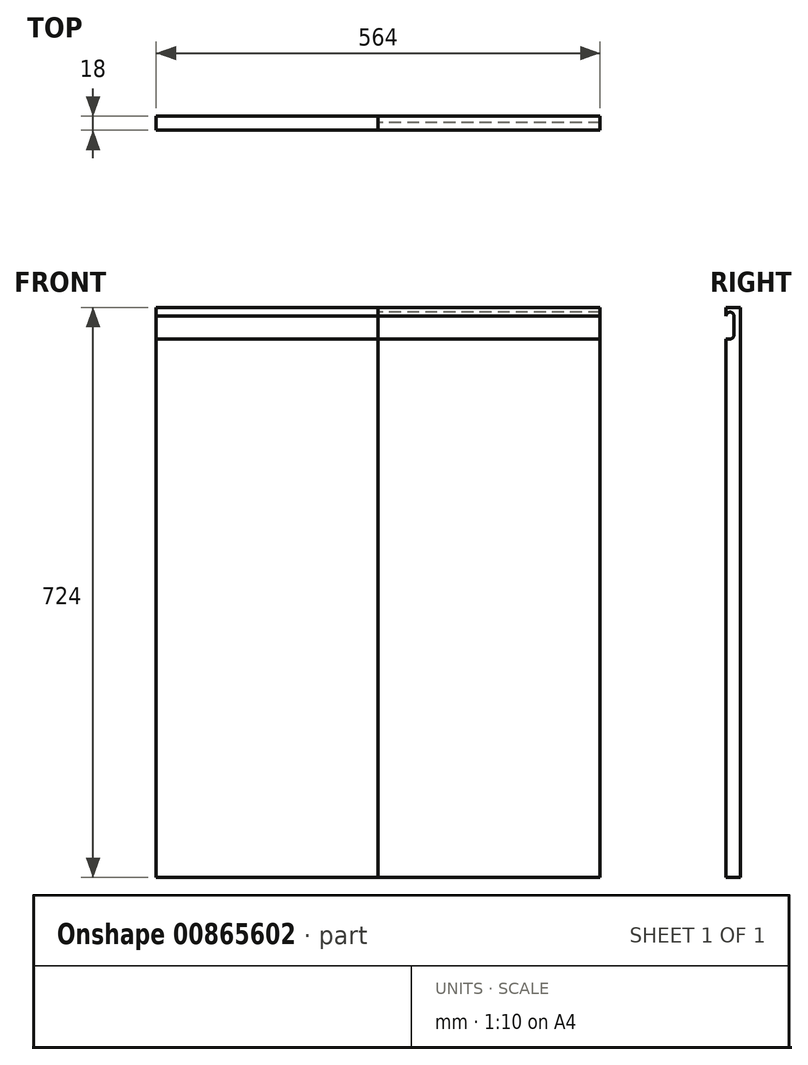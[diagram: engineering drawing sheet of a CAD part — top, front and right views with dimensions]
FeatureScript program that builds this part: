
annotation { "Feature Type Name" : "Feature", "Feature Type Description" : "" }
export const myFeature = defineFeature(function(context is Context, id is Id, definition is map)
    precondition{}
    {
        {
            var Q0;
            Q0=qCreatedBy(makeId("Front.planeOp"),FACE);
            var sketch = newSketch(context, id + "F0", { "sketchPlane" : qUnion([Q0])});
            skLineSegment(sketch, "E0.left", {"start": v(-331.36, 211.7) * mm, "end": v(-331.36, -512.3) * mm});
            skLineSegment(sketch, "E1", {"start": v(-613.36, -512.3) * mm, "end": v(-49.36, -512.3) * mm});
            skLineSegment(sketch, "E2", {"start": v(-613.36, 211.7) * mm, "end": v(-49.36, 211.7) * mm});
            skLineSegment(sketch, "E3", {"start": v(-49.36, 211.7) * mm, "end": v(-49.36, -512.3) * mm});
            skLineSegment(sketch, "E4", {"start": v(-613.36, 211.7) * mm, "end": v(-613.36, -512.3) * mm});
            skPoint(sketch, "E5.orphan", {"position": v(-631.36, 249.7) * mm});
            skSolve(sketch);
        }
        {
            var Q0;
            {var subQ0=sQuery(id+"F0.wireOp",EDGE,"E0.left");Q0=makeQuery(id+"F0.imprint","IMPRINT",FACE,{"disambiguationData":[TD([[makeQuery(id+"F0.imprint","IMPRINT",EDGE,{"derivedFrom":subQ0}),1.0]])]});}
            extrude(context, id + "F1", {"entities" : qUnion([Q0]), "depth" : 18 * mm, "offsetDistance" : 25 * mm});
        }
        {
            var Q0;
            Q0 = qSketchRegion(id + "F0", true);
            extrude(context, id + "F2", {"entities" : qUnion([Q0]), "depth" : 18 * mm, "offsetDistance" : 25 * mm});
        }
        {
            var Q0;
            Q0=makeQuery(id+"F2.opExtrude","SWEPT_FACE",FACE,{"disambiguationData":[OSD([sQuery(id+"F0.wireOp",EDGE,"E4")])]});
            var sketch = newSketch(context, id + "F3", { "sketchPlane" : qUnion([Q0])});
            skLineSegment(sketch, "E6", {"start": v(18, 171.7) * mm, "end": v(13, 171.7) * mm});
            skLineSegment(sketch, "E7", {"start": v(8, 176.7) * mm, "end": v(8, 200.7) * mm});
            skArc(sketch, "E8", {"start": v(18, 200.7) * mm, "mid": v(13, 205.7) * mm, "end": v(8, 200.7) * mm});
            skPoint(sketch, "E9.visualSharp", {"position": v(8, 171.7) * mm});
            skArc(sketch, "E9.filletArc", {"start": v(8, 176.7) * mm, "mid": v(9.46, 173.16) * mm, "end": v(13, 171.7) * mm});
            skSolve(sketch);
        }
        {
            var Q0;
            {var subQ1=sQuery(id+"F3.wireOp",EDGE,"E6");Q0=makeQuery(id+"F3.imprint","IMPRINT",FACE,{"disambiguationData":[TD([[makeQuery(id+"F3.imprint","IMPRINT",EDGE,{"derivedFrom":subQ1}),-1.0]])]});}
            extrude(context, id + "F4", {"entities" : qUnion([Q0]), "operationType" : NewBodyOperationType.REMOVE, "oppositeDirection" : true, "depth" : 661 * mm, "offsetDistance" : 25 * mm});
        }
    });
